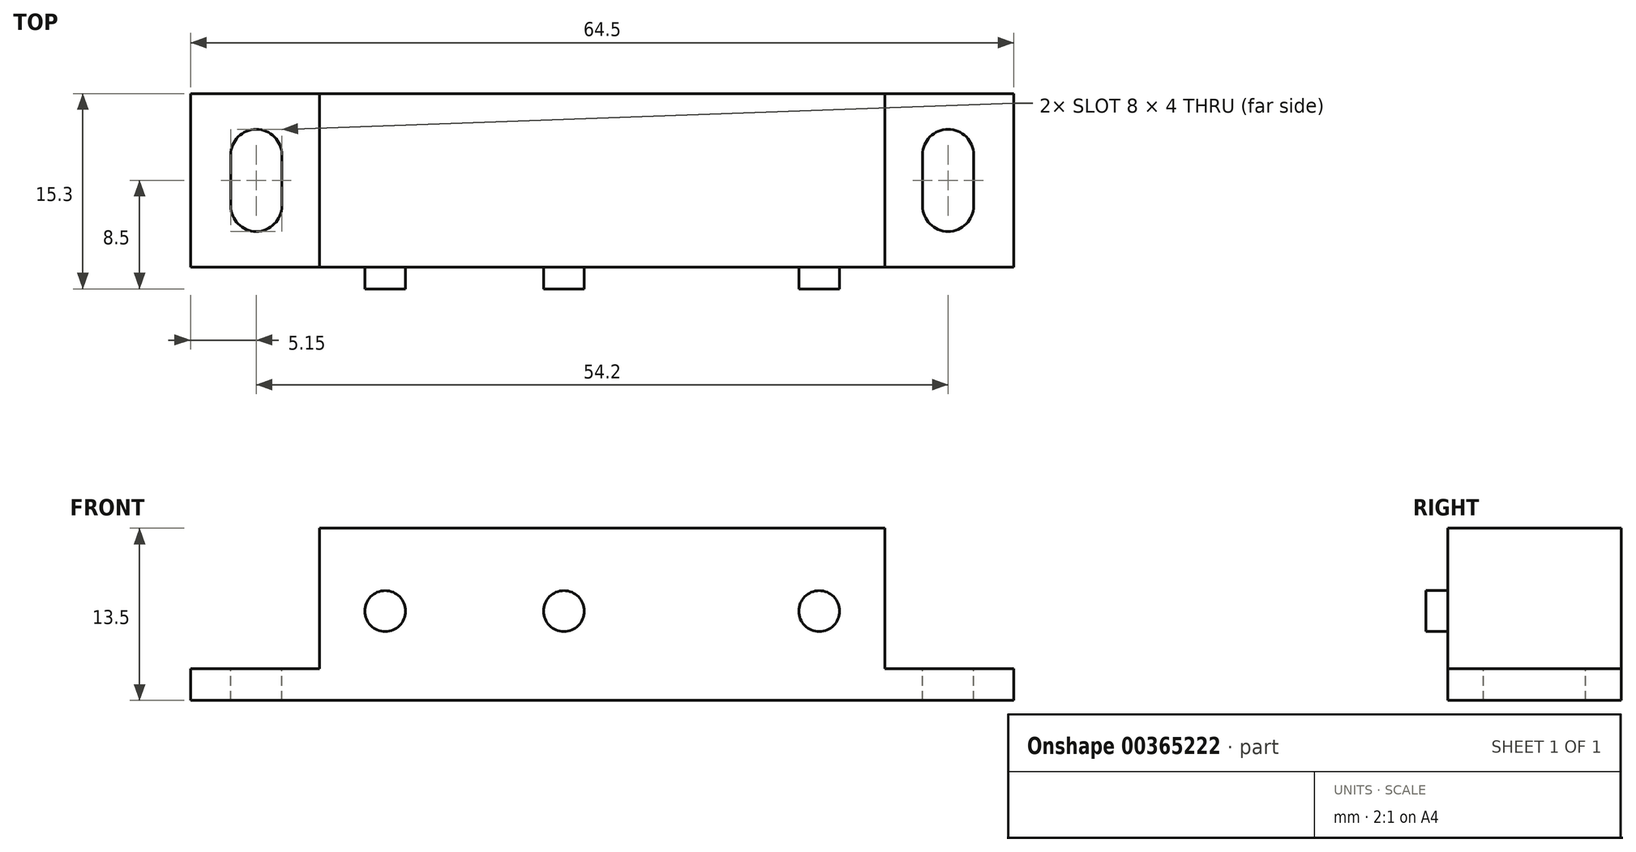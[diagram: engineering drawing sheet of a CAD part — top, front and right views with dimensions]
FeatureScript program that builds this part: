
annotation { "Feature Type Name" : "Feature", "Feature Type Description" : "" }
export const myFeature = defineFeature(function(context is Context, id is Id, definition is map)
    precondition{}
    {
        {
            var Q0;
            Q0=qCreatedBy(makeId("Front.planeOp"),FACE);
            var sketch = newSketch(context, id + "F0", { "sketchPlane" : qUnion([Q0])});
            skLineSegment(sketch, "E0.bottom", {"start": v(32.25, -6.75) * mm, "end": v(-32.25, -6.75) * mm});
            skLineSegment(sketch, "E0.top", {"start": v(32.25, 6.75) * mm, "end": v(-32.25, 6.75) * mm});
            skLineSegment(sketch, "E0.left", {"start": v(32.25, -6.75) * mm, "end": v(32.25, 6.75) * mm});
            skLineSegment(sketch, "E0.right", {"start": v(-32.25, -6.75) * mm, "end": v(-32.25, 6.75) * mm});
            skPoint(sketch, "E0.middle", {"position": v(0, 0) * mm});
            skSolve(sketch);
        }
        {
            var Q0;
            Q0 = qSketchRegion(id + "F0", true);
            extrude(context, id + "F1", {"entities" : qUnion([Q0]), "depth" : 13.6 * mm});
        }
        {
            var Q0;
            Q0=makeQuery(id+"F1.opExtrude","SWEPT_FACE",FACE,{"disambiguationData":[OSD([sQuery(id+"F0.wireOp",EDGE,"E0.top")])]});
            var sketch = newSketch(context, id + "F2", { "sketchPlane" : qUnion([Q0])});
            skLineSegment(sketch, "E1.left", {"start": v(22.15, -13.6) * mm, "end": v(22.15, 0) * mm});
            skLineSegment(sketch, "E1.right", {"start": v(-22.15, -13.6) * mm, "end": v(-22.15, 0) * mm});
            skPoint(sketch, "E1.middle", {"position": v(0, -6.8) * mm});
            skPoint(sketch, "E1.middle.positionSnap0", {"position": v(-32.25, -6.8) * mm});
            skPoint(sketch, "E1.centerSnap0", {"position": v(-32.25, -6.8) * mm});
            skLineSegment(sketch, "E2.bottom", {"start": v(22.15, 0) * mm, "end": v(32.25, 0) * mm});
            skLineSegment(sketch, "E2.top", {"start": v(22.15, -13.6) * mm, "end": v(32.25, -13.6) * mm});
            skLineSegment(sketch, "E2.left", {"start": v(22.15, 0) * mm, "end": v(22.15, -13.6) * mm});
            skLineSegment(sketch, "E2.right", {"start": v(32.25, 0) * mm, "end": v(32.25, -13.6) * mm});
            skLineSegment(sketch, "E3.bottom", {"start": v(-22.15, 0) * mm, "end": v(-32.25, 0) * mm});
            skLineSegment(sketch, "E3.top", {"start": v(-22.15, -13.6) * mm, "end": v(-32.25, -13.6) * mm});
            skLineSegment(sketch, "E3.left", {"start": v(-22.15, 0) * mm, "end": v(-22.15, -13.6) * mm});
            skLineSegment(sketch, "E3.right", {"start": v(-32.25, 0) * mm, "end": v(-32.25, -13.6) * mm});
            skSolve(sketch);
        }
        {
            var Q0;
            Q0=makeQuery(id+"F2.imprint","IMPRINT",FACE,{"disambiguationData":[TD([[makeQuery(id+"F2.imprint","IMPRINT",EDGE,{"derivedFrom":sQuery(id+"F2.wireOp",EDGE,"E3.bottom")}),1.0]])]});
            var Q1;
            Q1=makeQuery(id+"F2.imprint","IMPRINT",FACE,{"disambiguationData":[TD([[makeQuery(id+"F2.imprint","IMPRINT",EDGE,{"derivedFrom":sQuery(id+"F2.wireOp",EDGE,"E2.bottom")}),1.0]])]});
            extrude(context, id + "F3", {"entities" : qUnion([Q0, Q1]), "operationType" : NewBodyOperationType.REMOVE, "oppositeDirection" : true, "depth" : 11 * mm});
        }
        {
            var Q0;
            Q0=makeQuery(id+"F1.opExtrude","CAP_FACE",FACE,{"disambiguationData":[OSD([sQuery(id+"F0.wireOp",EDGE,"E0.bottom"),sQuery(id+"F0.wireOp",EDGE,"E0.top"),sQuery(id+"F0.wireOp",EDGE,"E0.left"),sQuery(id+"F0.wireOp",EDGE,"E0.right")])],"isStart":false});
            var sketch = newSketch(context, id + "F4", { "sketchPlane" : qUnion([Q0])});
            skLineSegment(sketch, "E4", {"start": v(22.15, -4.25) * mm, "end": v(17, -4.25) * mm, "construction": true});
            skLineSegment(sketch, "E5", {"start": v(17, -6.75) * mm, "end": v(17, 0.25) * mm, "construction": true});
            skCircle(sketch, "E6", {"center": v(17, 0.25) * mm, "radius": 1.6 * mm});
            skLineSegment(sketch, "E7", {"start": v(17, 0.25) * mm, "end": v(-3, 0.25) * mm, "construction": true});
            skCircle(sketch, "E8", {"center": v(-3, 0.25) * mm, "radius": 1.6 * mm});
            skLineSegment(sketch, "E9", {"start": v(-3, 0.25) * mm, "end": v(-17, 0.25) * mm, "construction": true});
            skCircle(sketch, "E10", {"center": v(-17, 0.25) * mm, "radius": 1.6 * mm});
            skSolve(sketch);
        }
        {
            var Q0;
            Q0 = qSketchRegion(id + "F4", true);
            extrude(context, id + "F5", {"entities" : qUnion([Q0]), "operationType" : NewBodyOperationType.ADD, "depth" : 1.7 * mm});
        }
        {
            var Q0;
            Q0=makeQuery(id+"F3.boolean.opBoolean","COPY",FACE,{"derivedFrom":makeQuery(id+"F3.opExtrude","CAP_FACE",FACE,{"disambiguationData":[OSD([sQuery(id+"F2.wireOp",EDGE,"E2.bottom"),sQuery(id+"F2.wireOp",EDGE,"E2.top"),sQuery(id+"F2.wireOp",EDGE,"E2.left"),sQuery(id+"F2.wireOp",EDGE,"E2.right")])],"isStart":false})});
            var sketch = newSketch(context, id + "F6", { "sketchPlane" : qUnion([Q0])});
            skLineSegment(sketch, "E11.0.0", {"start": v(22.15, -13.6) * mm, "end": v(22.15, 0) * mm, "construction": true});
            skLineSegment(sketch, "E11.0.1", {"start": v(22.15, 0) * mm, "end": v(-22.15, 0) * mm, "construction": true});
            skLineSegment(sketch, "E11.0.2", {"start": v(-22.15, 0) * mm, "end": v(-22.15, -13.6) * mm, "construction": true});
            skLineSegment(sketch, "E11.0.3", {"start": v(-22.15, -13.6) * mm, "end": v(22.15, -13.6) * mm, "construction": true});
            skLineSegment(sketch, "E12.bottom", {"start": v(27.1, -8.8) * mm, "end": v(-27.1, -8.8) * mm, "construction": true});
            skLineSegment(sketch, "E12.top", {"start": v(27.1, -4.8) * mm, "end": v(-27.1, -4.8) * mm, "construction": true});
            skLineSegment(sketch, "E12.left", {"start": v(27.1, -8.8) * mm, "end": v(27.1, -4.8) * mm, "construction": true});
            skLineSegment(sketch, "E12.right", {"start": v(-27.1, -8.8) * mm, "end": v(-27.1, -4.8) * mm, "construction": true});
            skPoint(sketch, "E12.middle", {"position": v(0, -6.8) * mm});
            skPoint(sketch, "E12.middle.positionSnap0", {"position": v(-22.15, -6.8) * mm});
            skPoint(sketch, "E12.middle.positionSnap1", {"position": v(0, 0) * mm});
            skPoint(sketch, "E12.centerSnap0", {"position": v(-22.15, -6.8) * mm});
            skPoint(sketch, "E12.centerSnap1", {"position": v(0, 0) * mm});
            skLineSegment(sketch, "E13.bottom", {"start": v(-25.1, -8.8) * mm, "end": v(-29.1, -8.8) * mm, "construction": true});
            skLineSegment(sketch, "E13.top", {"start": v(-25.1, -4.8) * mm, "end": v(-29.1, -4.8) * mm, "construction": true});
            skLineSegment(sketch, "E13.left", {"start": v(-25.1, -8.8) * mm, "end": v(-25.1, -4.8) * mm, "construction": true});
            skLineSegment(sketch, "E13.right", {"start": v(-29.1, -8.8) * mm, "end": v(-29.1, -4.8) * mm, "construction": true});
            skPoint(sketch, "E13.middle", {"position": v(-27.1, -6.8) * mm});
            skArc(sketch, "E14", {"start": v(-29.1, -4.8) * mm, "mid": v(-27.1, -2.8) * mm, "end": v(-25.1, -4.8) * mm});
            skLineSegment(sketch, "E15", {"start": v(-29.1, -4.8) * mm, "end": v(-29.1, -6.8) * mm});
            skLineSegment(sketch, "E16", {"start": v(-25.1, -4.8) * mm, "end": v(-25.1, -6.8) * mm});
            skLineSegment(sketch, "E17", {"start": v(-27.1, -6.8) * mm, "end": v(-32.93, -6.8) * mm, "construction": true});
            skLineSegment(sketch, "E18.MirrorCS", {"start": v(-29.1, -4.8) * mm, "end": v(-29.1, -8.8) * mm});
            skArc(sketch, "E19.MirrorCS", {"start": v(-29.1, -8.8) * mm, "mid": v(-27.1, -10.8) * mm, "end": v(-25.1, -8.8) * mm});
            skLineSegment(sketch, "E20.MirrorCS", {"start": v(-25.1, -4.8) * mm, "end": v(-25.1, -8.8) * mm});
            skArc(sketch, "E21.MirrorCS", {"start": v(29.1, -4.8) * mm, "mid": v(27.1, -2.8) * mm, "end": v(25.1, -4.8) * mm});
            skLineSegment(sketch, "E22.MirrorCS", {"start": v(25.1, -4.8) * mm, "end": v(25.1, -8.8) * mm});
            skArc(sketch, "E23.MirrorCS", {"start": v(29.1, -8.8) * mm, "mid": v(27.1, -10.8) * mm, "end": v(25.1, -8.8) * mm});
            skLineSegment(sketch, "E24.MirrorCS", {"start": v(29.1, -4.8) * mm, "end": v(29.1, -8.8) * mm});
            skSolve(sketch);
        }
        {
            var Q0;
            Q0 = qSketchRegion(id + "F6", true);
            extrude(context, id + "F7", {"entities" : qUnion([Q0]), "operationType" : NewBodyOperationType.REMOVE, "oppositeDirection" : true, "depth" : 25 * mm});
        }
    });
